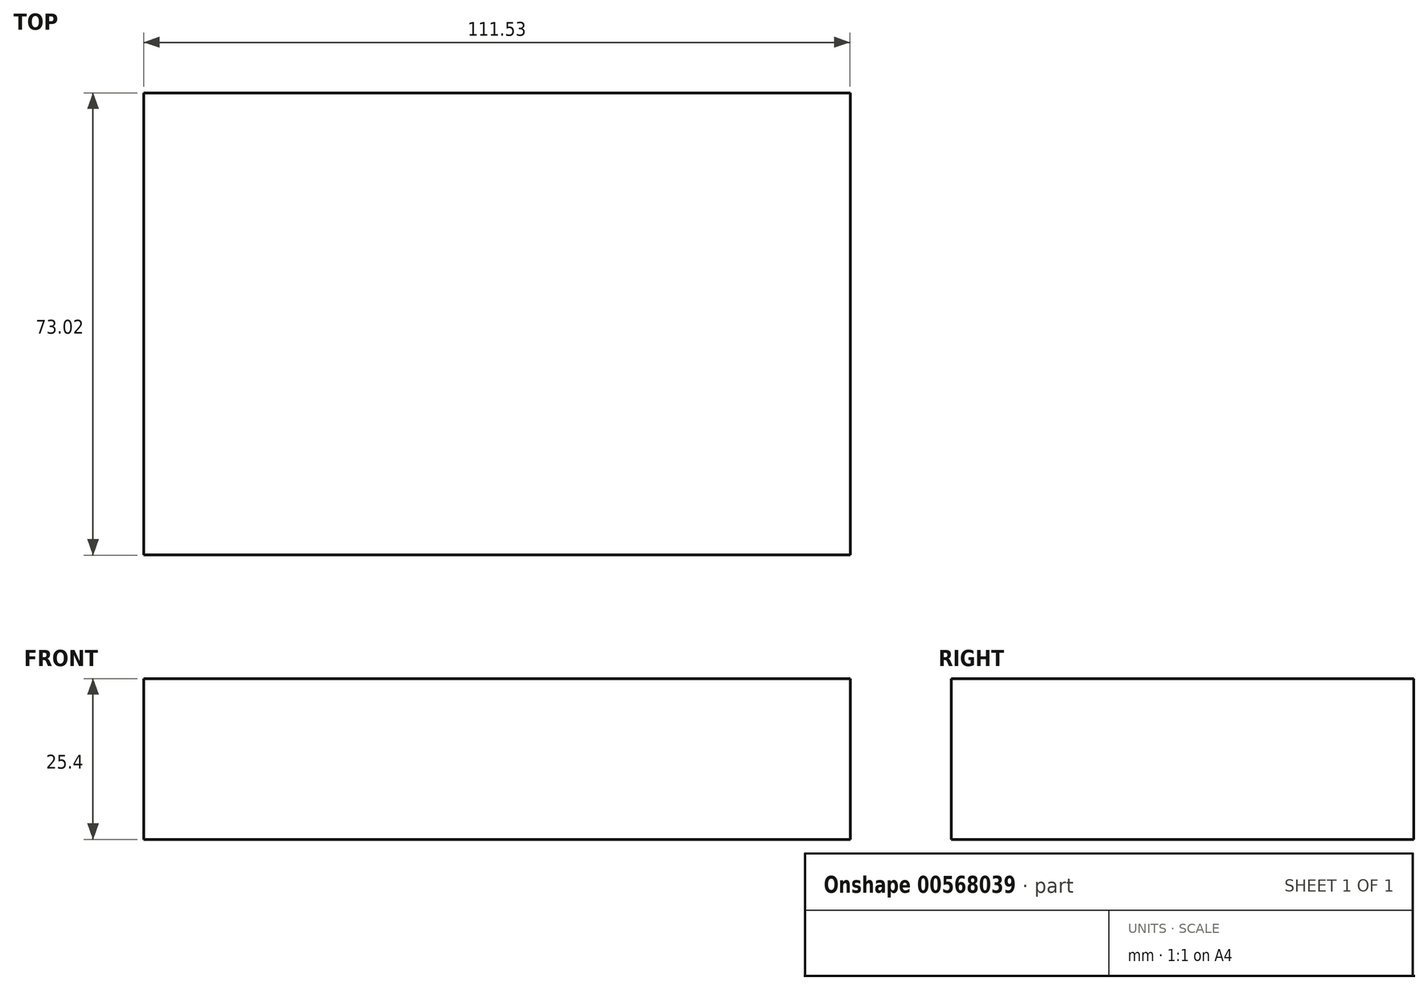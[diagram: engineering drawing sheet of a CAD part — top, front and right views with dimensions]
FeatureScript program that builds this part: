
annotation { "Feature Type Name" : "Feature", "Feature Type Description" : "" }
export const myFeature = defineFeature(function(context is Context, id is Id, definition is map)
    precondition{}
    {
        {
            var Q0;
            Q0=qCreatedBy(makeId("Top.planeOp"),FACE);
            var sketch = newSketch(context, id + "F0", { "sketchPlane" : qUnion([Q0])});
            skLineSegment(sketch, "E0.bottom", {"start": v(-51.7, 39.84) * mm, "end": v(59.83, 39.84) * mm});
            skLineSegment(sketch, "E0.top", {"start": v(-51.7, -33.18) * mm, "end": v(59.83, -33.18) * mm});
            skLineSegment(sketch, "E0.left", {"start": v(-51.7, 39.84) * mm, "end": v(-51.7, -33.18) * mm});
            skLineSegment(sketch, "E0.right", {"start": v(59.83, 39.84) * mm, "end": v(59.83, -33.18) * mm});
            skSolve(sketch);
        }
        {
            var Q0;
            Q0=makeQuery(id+"F0.imprint","IMPRINT",FACE,{"disambiguationData":[TD([[makeQuery(id+"F0.imprint","IMPRINT",EDGE,{"derivedFrom":sQuery(id+"F0.wireOp",EDGE,"E0.bottom")}),-1.0]])]});
            extrude(context, id + "F1", {"entities" : qUnion([Q0]), "depth" : 25.4 * mm, "offsetDistance" : 25.4 * mm});
        }
    });
